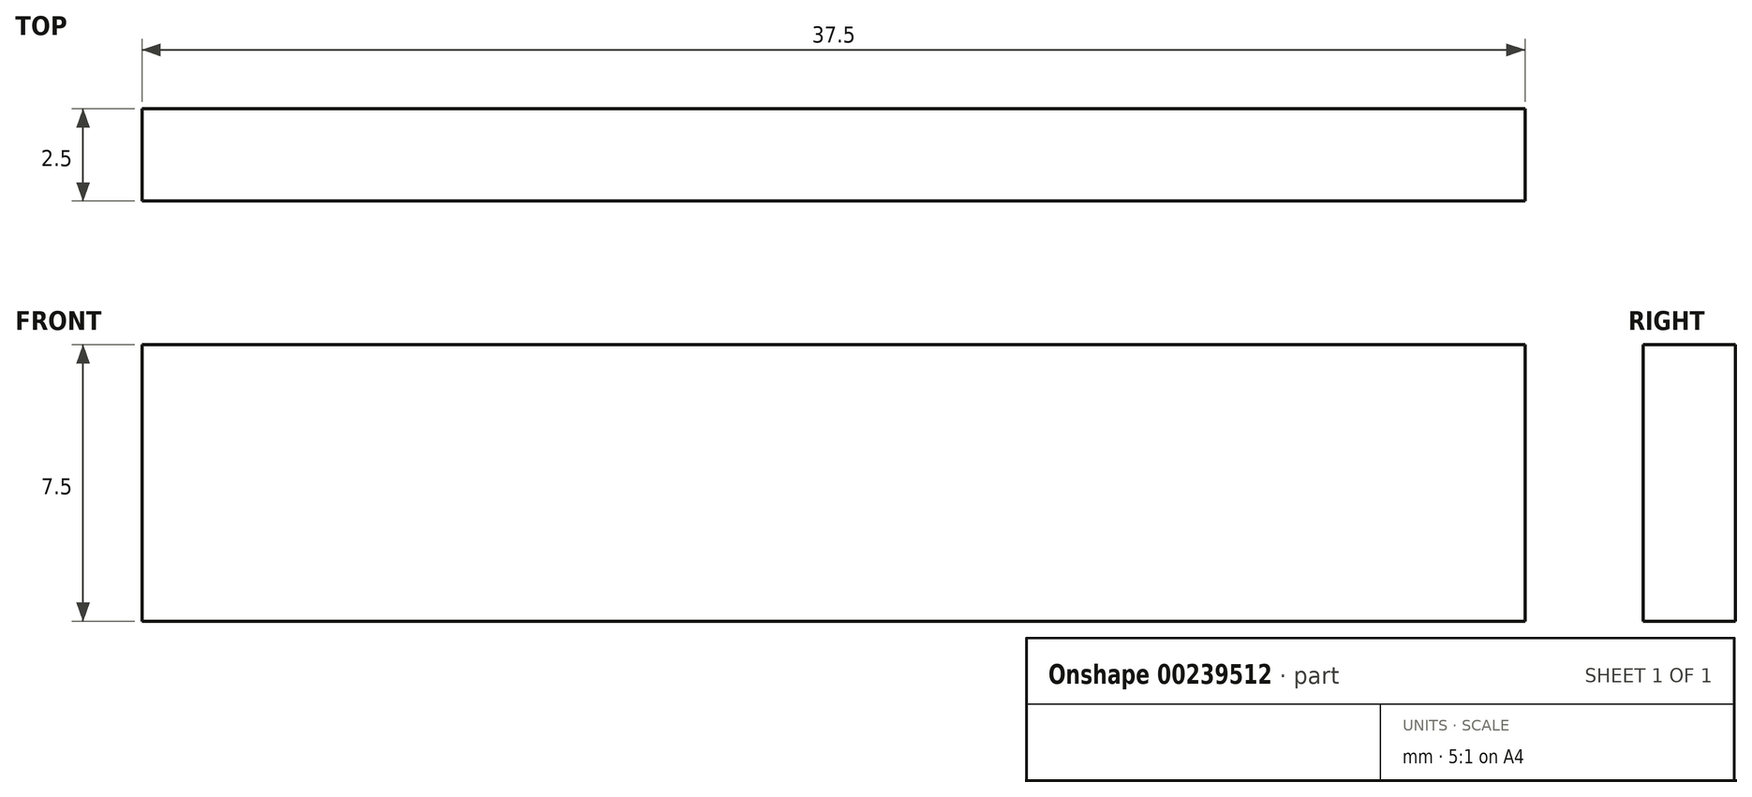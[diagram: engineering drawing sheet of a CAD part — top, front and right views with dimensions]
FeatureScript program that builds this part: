
annotation { "Feature Type Name" : "Feature", "Feature Type Description" : "" }
export const myFeature = defineFeature(function(context is Context, id is Id, definition is map)
    precondition{}
    {
        {
            var Q0;
            Q0=qCreatedBy(makeId("Top.planeOp"),FACE);
            var sketch = newSketch(context, id + "F0", { "sketchPlane" : qUnion([Q0])});
            skLineSegment(sketch, "E0.bottom", {"start": v(18.75, -1.25) * mm, "end": v(-18.75, -1.25) * mm});
            skLineSegment(sketch, "E0.top", {"start": v(18.75, 1.25) * mm, "end": v(-18.75, 1.25) * mm});
            skLineSegment(sketch, "E0.left", {"start": v(18.75, -1.25) * mm, "end": v(18.75, 1.25) * mm});
            skLineSegment(sketch, "E0.right", {"start": v(-18.75, -1.25) * mm, "end": v(-18.75, 1.25) * mm});
            skPoint(sketch, "E0.middle", {"position": v(0, 0) * mm});
            skSolve(sketch);
        }
        {
            var Q0;
            Q0 = qSketchRegion(id + "F0", true);
            extrude(context, id + "F1", {"entities" : qUnion([Q0]), "endBound" : BoundingType.SYMMETRIC, "depth" : 7.5 * mm});
        }
    });
